# Revit family: Storage-Freestanding-Teknion-JNFBS_Beam_Tower_with_Solid_Door-R2016
name_source: partatom
category: Furniture
revit_build: Autodesk Revit Architecture 2016 (Build: 20150714_1515(x64)
units: mm (PartAtom-declared; Revit-internal decimal feet)

## family parameters
Always vertical = Yes
Cut with Voids When Loaded = No
OmniClass Number = 23.40.20.00
OmniClass Title = General Furniture and Specialties
Room Calculation Point = No
Shared = Yes
Work Plane-Based = No

## types (4) — shared parameters
Assembly Code = E2020200
Manufacturer = Teknion
Manufacturer Fax = 416.661.4586
Part Number = JNFBS
Product Documentation Link = http://www.teknion.com
Product Line = CityLine
Product Page URL = http://www.teknion.com
Series = CityLine
Sustainability Data = http://www.teknion.com
URL = www.teknion.com
Unit Weight URL = http://www.teknion.com
Warranty = http://www.teknion.com

## per-type parameters (varying)
| type | Description | End of Station | End of Station Offset | In-Line | Model |
| End of Station W/ Shelves | Beam Tower with Full Solid Door - Shelves, End of Station | Yes | 1.016 " | No | JNFBSSS___E |
| In-Line W/ Shelves | Beam Tower with Full Solid Door - Shelves, In-Line Position | No | 0 " | Yes | JNFBSSS___I |
| In-Line W/ Wardrobe | Beam Tower with Full Solid Door - Wardrobe, In-Line Position | No | 0 " | Yes | JNFBSSW___I |
| End of Station W/ Wardrobe | Beam Tower with Full Solid Door - Wardrobe, End of Station | Yes | 1.016 " | No | JNFBSSW___E |

## geometry (parser evidence)
native form markers: Sweep x2
no freeform markers — native parametric forms only
